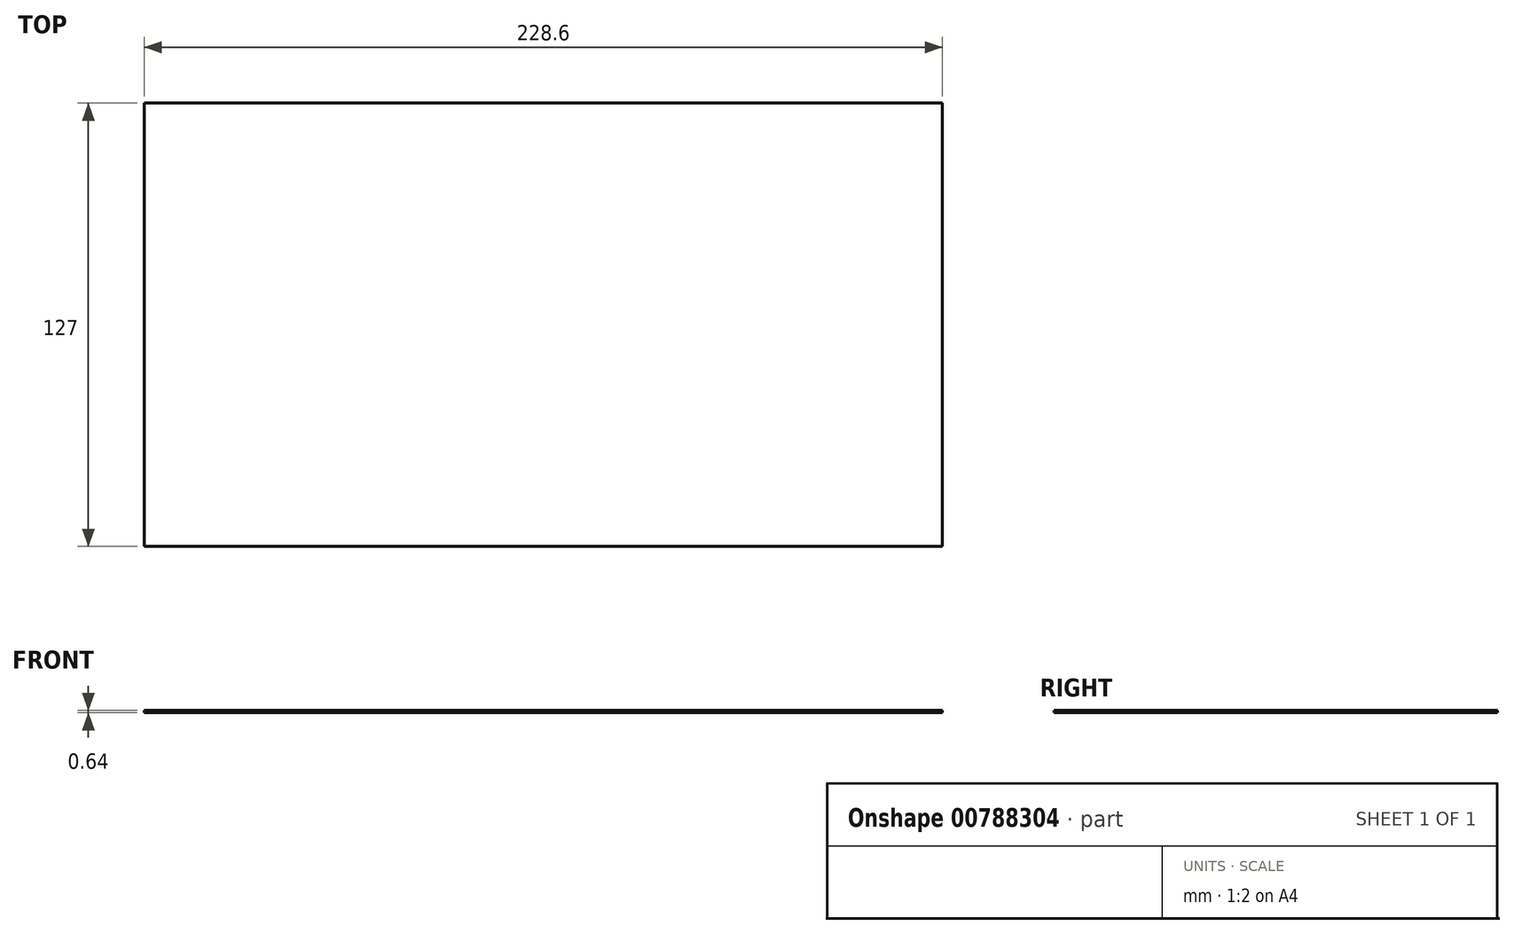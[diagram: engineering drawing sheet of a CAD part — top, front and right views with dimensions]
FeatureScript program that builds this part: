
annotation { "Feature Type Name" : "Feature", "Feature Type Description" : "" }
export const myFeature = defineFeature(function(context is Context, id is Id, definition is map)
    precondition{}
    {
        {
            var Q0;
            Q0=qCreatedBy(makeId("Top.planeOp"),FACE);
            var sketch = newSketch(context, id + "F0", { "sketchPlane" : qUnion([Q0])});
            skLineSegment(sketch, "E0.bottom", {"start": v(114.3, 63.5) * mm, "end": v(-114.3, 63.5) * mm});
            skLineSegment(sketch, "E0.top", {"start": v(114.3, -63.5) * mm, "end": v(-114.3, -63.5) * mm});
            skLineSegment(sketch, "E0.left", {"start": v(114.3, 63.5) * mm, "end": v(114.3, -63.5) * mm});
            skLineSegment(sketch, "E0.right", {"start": v(-114.3, 63.5) * mm, "end": v(-114.3, -63.5) * mm});
            skPoint(sketch, "E0.middle", {"position": v(0, 0) * mm});
            skSolve(sketch);
        }
        {
            var Q0;
            Q0=makeQuery(id+"F0.imprint","IMPRINT",FACE,{"disambiguationData":[TD([[makeQuery(id+"F0.imprint","IMPRINT",EDGE,{"derivedFrom":sQuery(id+"F0.wireOp",EDGE,"E0.bottom")}),1.0]])]});
            extrude(context, id + "F1", {"entities" : qUnion([Q0]), "depth" : 0.64 * mm, "offsetDistance" : 25.4 * mm});
        }
    });
